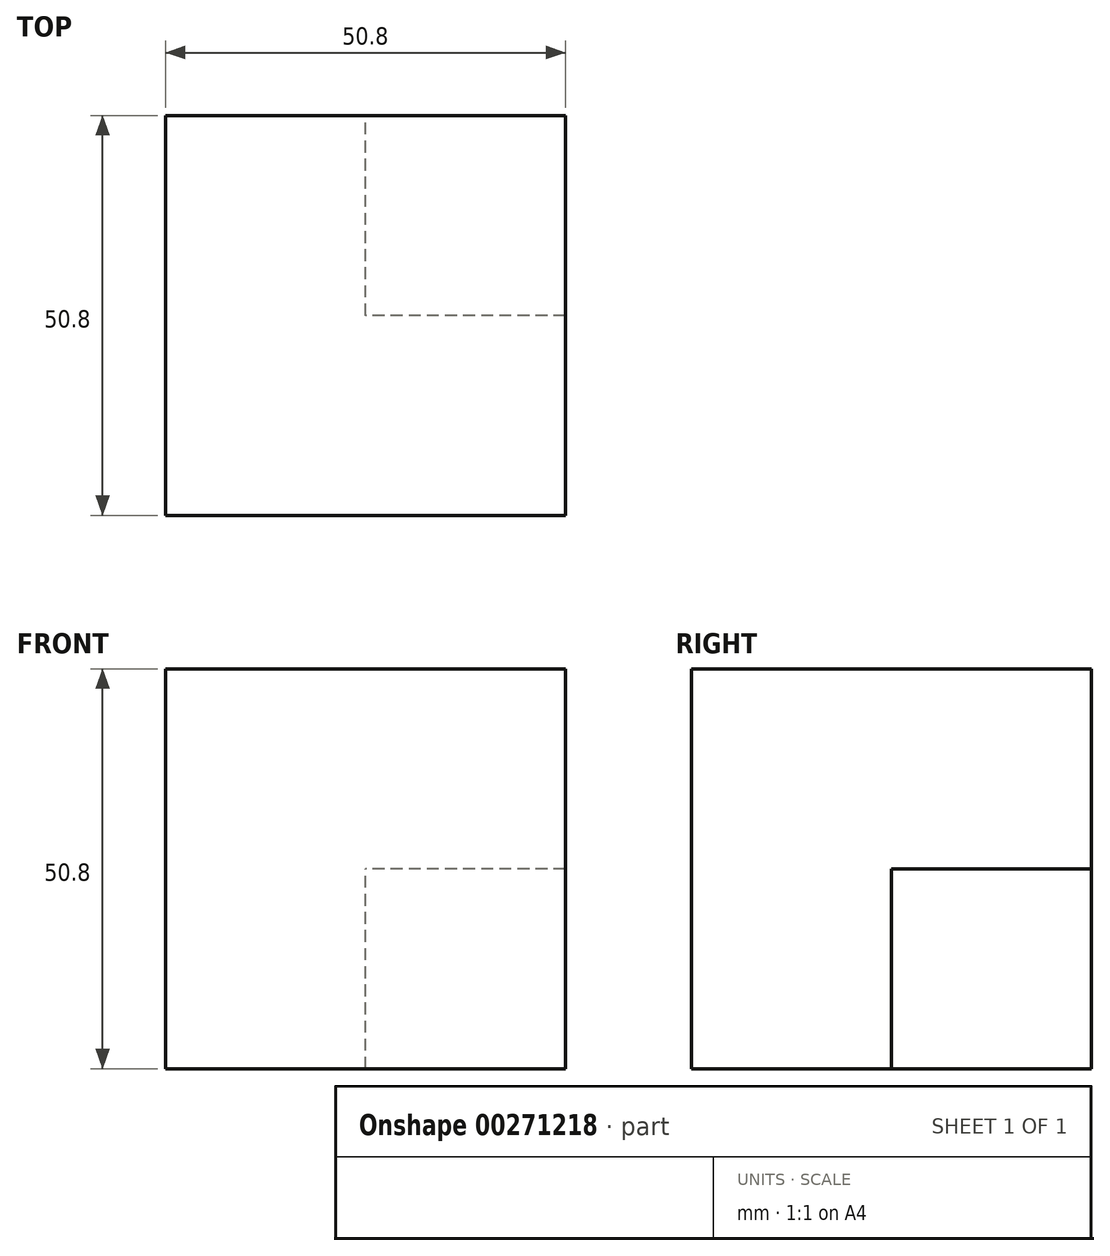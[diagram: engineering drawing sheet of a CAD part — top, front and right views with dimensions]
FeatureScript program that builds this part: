
annotation { "Feature Type Name" : "Feature", "Feature Type Description" : "" }
export const myFeature = defineFeature(function(context is Context, id is Id, definition is map)
    precondition{}
    {
        {
            var Q0;
            Q0=qCreatedBy(makeId("Front.planeOp"),FACE);
            var sketch = newSketch(context, id + "F0", { "sketchPlane" : qUnion([Q0])});
            skLineSegment(sketch, "E0.bottom", {"start": v(0, 0) * mm, "end": v(-50.8, 0) * mm});
            skLineSegment(sketch, "E0.top", {"start": v(0, 50.8) * mm, "end": v(-50.8, 50.8) * mm});
            skLineSegment(sketch, "E0.left", {"start": v(0, 0) * mm, "end": v(0, 50.8) * mm});
            skLineSegment(sketch, "E0.right", {"start": v(-50.8, 0) * mm, "end": v(-50.8, 50.8) * mm});
            skLineSegment(sketch, "E1.bottom", {"start": v(0, 0) * mm, "end": v(-25.4, 0) * mm});
            skLineSegment(sketch, "E1.left", {"start": v(0, 0) * mm, "end": v(0, 25.4) * mm});
            skSolve(sketch);
        }
        {
            var Q0;
            Q0=makeQuery(id+"F0.imprint","IMPRINT",FACE,{"disambiguationData":[TD([[makeQuery(id+"F0.imprint","IMPRINT",EDGE,{"derivedFrom":sQuery(id+"F0.wireOp",EDGE,"E0.bottom")}),-1.0]])]});
            var sketch = newSketch(context, id + "F1", { "sketchPlane" : qUnion([Q0])});
            skLineSegment(sketch, "E2.bottom", {"start": v(0, 0) * mm, "end": v(-25.4, 0) * mm});
            skLineSegment(sketch, "E2.top", {"start": v(0, 25.4) * mm, "end": v(-25.4, 25.4) * mm});
            skLineSegment(sketch, "E2.left", {"start": v(0, 0) * mm, "end": v(0, 25.4) * mm});
            skLineSegment(sketch, "E2.right", {"start": v(-25.4, 0) * mm, "end": v(-25.4, 25.4) * mm});
            skSolve(sketch);
        }
        {
            var Q0;
            Q0 = qSketchRegion(id + "F0", true);
            extrude(context, id + "F2", {"entities" : qUnion([Q0]), "depth" : 50.8 * mm});
        }
        {
            var Q0;
            Q0 = qSketchRegion(id + "F1", true);
            extrude(context, id + "F3", {"entities" : qUnion([Q0]), "operationType" : NewBodyOperationType.REMOVE, "depth" : 25.4 * mm});
        }
    });
